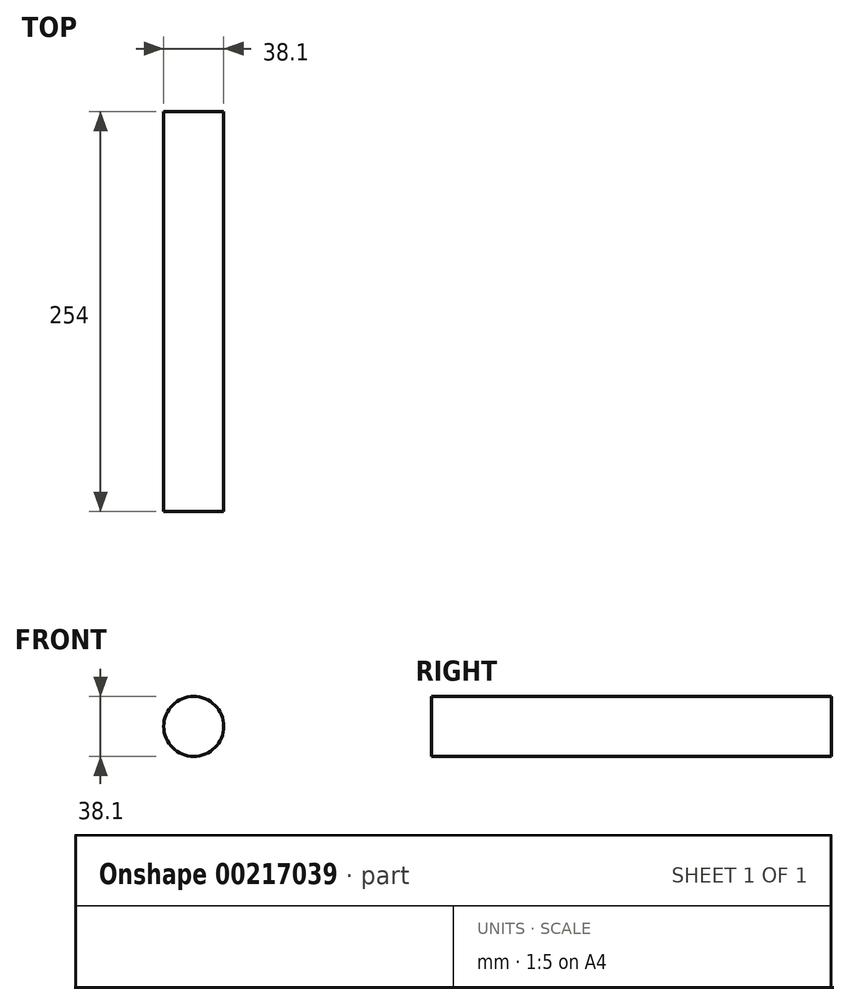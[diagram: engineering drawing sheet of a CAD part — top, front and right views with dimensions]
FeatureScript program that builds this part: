
annotation { "Feature Type Name" : "Feature", "Feature Type Description" : "" }
export const myFeature = defineFeature(function(context is Context, id is Id, definition is map)
    precondition{}
    {
        {
            var Q0;
            Q0=qCreatedBy(makeId("Front.planeOp"),FACE);
            var sketch = newSketch(context, id + "F0", { "sketchPlane" : qUnion([Q0])});
            skCircle(sketch, "E0", {"center": v(0, 0) * mm, "radius": 19.05 * mm});
            skSolve(sketch);
        }
        {
            var Q0;
            Q0=makeQuery(id+"F0.imprint","IMPRINT",FACE,{"disambiguationData":[TD([[makeQuery(id+"F0.imprint","IMPRINT",EDGE,{"derivedFrom":sQuery(id+"F0.wireOp",EDGE,"E0")}),1.0]])]});
            extrude(context, id + "F1", {"entities" : qUnion([Q0]), "depth" : 254 * mm});
        }
    });
